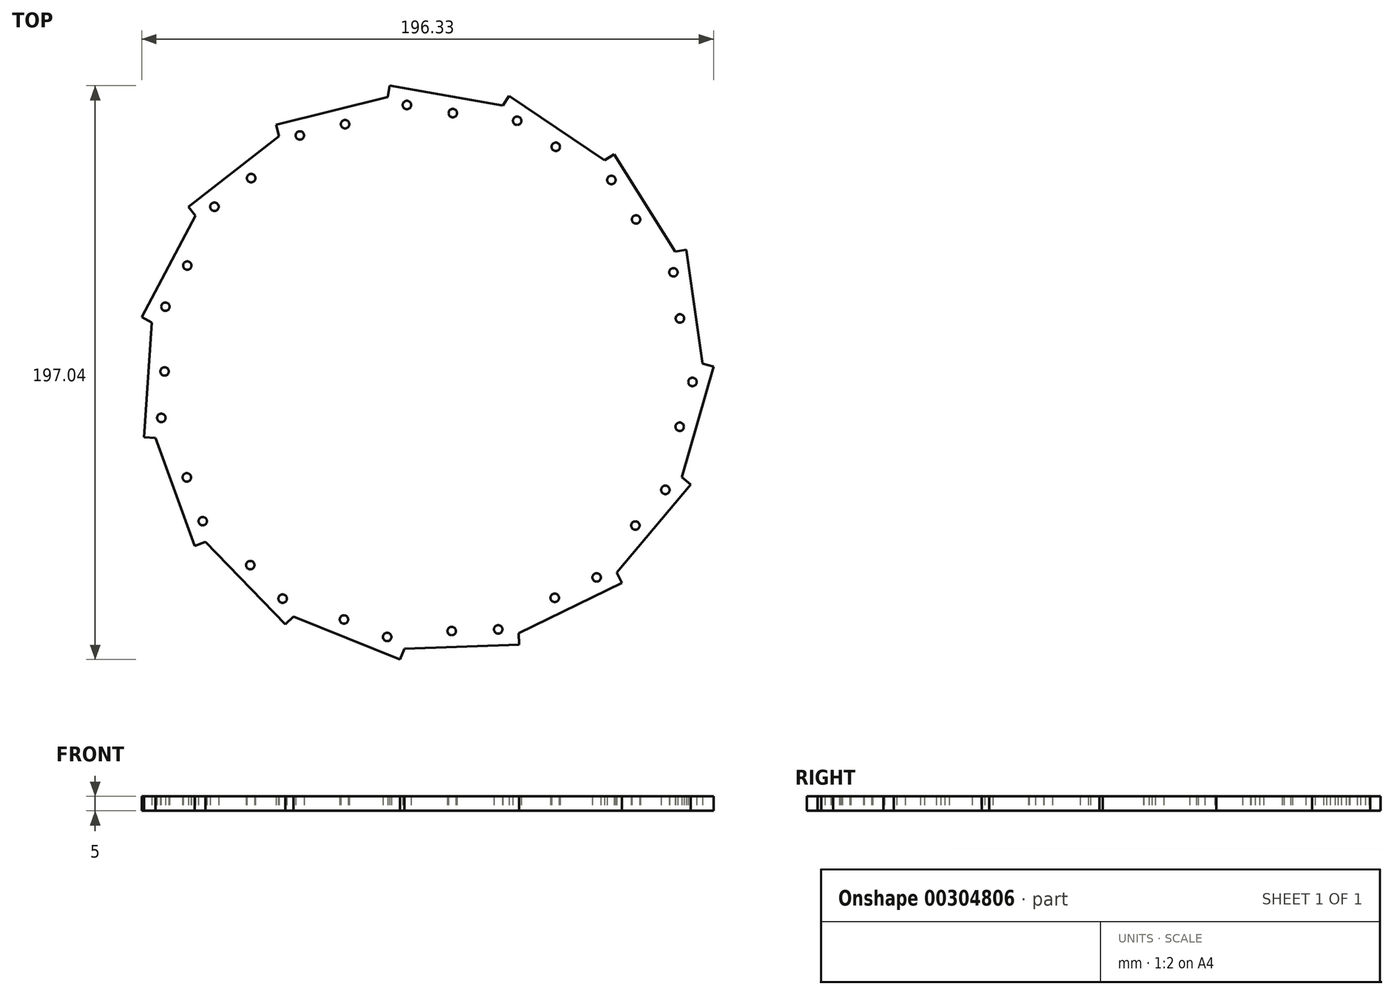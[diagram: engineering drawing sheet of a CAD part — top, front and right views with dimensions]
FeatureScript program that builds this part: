
annotation { "Feature Type Name" : "Feature", "Feature Type Description" : "" }
export const myFeature = defineFeature(function(context is Context, id is Id, definition is map)
    precondition{}
    {
        {
            var Q0;
            Q0=qCreatedBy(makeId("Top.planeOp"),FACE);
            var sketch = newSketch(context, id + "F0", { "sketchPlane" : qUnion([Q0])});
            skCircle(sketch, "E0.1.6", {"center": v(-42.97, 81.25) * mm, "radius": 1.45 * mm});
            skCircle(sketch, "E0.1.14", {"center": v(-27.44, 85.12) * mm, "radius": 1.45 * mm});
            skPoint(sketch, "E0.center", {"position": v(0, 0) * mm});
            skLineSegment(sketch, "E1", {"start": v(-51.1, 84.9) * mm, "end": v(-12.83, 94.43) * mm});
            skLineSegment(sketch, "E2", {"start": v(-12.83, 94.43) * mm, "end": v(-12.15, 98.33) * mm});
            skLineSegment(sketch, "E3.1.0", {"start": v(-81.2, 56.77) * mm, "end": v(-50.13, 81.04) * mm});
            skCircle(sketch, "E3.1.1", {"center": v(-72.3, 56.75) * mm, "radius": 1.45 * mm});
            skCircle(sketch, "E3.1.2", {"center": v(-59.7, 66.6) * mm, "radius": 1.45 * mm});
            skLineSegment(sketch, "E3.1.3", {"start": v(-50.13, 81.04) * mm, "end": v(-51.1, 84.9) * mm});
            skLineSegment(sketch, "E3.2.0", {"start": v(-97.27, 18.83) * mm, "end": v(-78.76, 53.65) * mm});
            skCircle(sketch, "E3.2.1", {"center": v(-89.13, 22.43) * mm, "radius": 1.45 * mm});
            skCircle(sketch, "E3.2.2", {"center": v(-81.62, 36.56) * mm, "radius": 1.45 * mm});
            skLineSegment(sketch, "E3.2.3", {"start": v(-78.76, 53.65) * mm, "end": v(-81.2, 56.77) * mm});
            skLineSegment(sketch, "E3.3.0", {"start": v(-96.52, -22.36) * mm, "end": v(-93.77, 16.97) * mm});
            skCircle(sketch, "E3.3.1", {"center": v(-90.55, -15.76) * mm, "radius": 1.45 * mm});
            skCircle(sketch, "E3.3.2", {"center": v(-89.43, 0.2) * mm, "radius": 1.45 * mm});
            skLineSegment(sketch, "E3.3.3", {"start": v(-93.77, 16.97) * mm, "end": v(-97.27, 18.83) * mm});
            skLineSegment(sketch, "E3.4.0", {"start": v(-79.08, -59.69) * mm, "end": v(-92.57, -22.63) * mm});
            skCircle(sketch, "E3.4.1", {"center": v(-76.31, -51.23) * mm, "radius": 1.45 * mm});
            skCircle(sketch, "E3.4.2", {"center": v(-81.78, -36.2) * mm, "radius": 1.45 * mm});
            skLineSegment(sketch, "E3.4.3", {"start": v(-92.57, -22.63) * mm, "end": v(-96.52, -22.36) * mm});
            skLineSegment(sketch, "E3.5.0", {"start": v(-47.97, -86.7) * mm, "end": v(-75.36, -58.33) * mm});
            skCircle(sketch, "E3.5.1", {"center": v(-48.88, -77.84) * mm, "radius": 1.45 * mm});
            skCircle(sketch, "E3.5.2", {"center": v(-60, -66.33) * mm, "radius": 1.45 * mm});
            skLineSegment(sketch, "E3.5.3", {"start": v(-75.36, -58.33) * mm, "end": v(-79.08, -59.69) * mm});
            skLineSegment(sketch, "E3.6.0", {"start": v(-8.56, -98.7) * mm, "end": v(-45.12, -83.94) * mm});
            skCircle(sketch, "E3.6.1", {"center": v(-13, -90.99) * mm, "radius": 1.45 * mm});
            skCircle(sketch, "E3.6.2", {"center": v(-27.83, -85) * mm, "radius": 1.45 * mm});
            skLineSegment(sketch, "E3.6.3", {"start": v(-45.12, -83.94) * mm, "end": v(-47.97, -86.7) * mm});
            skLineSegment(sketch, "E3.7.0", {"start": v(32.33, -93.66) * mm, "end": v(-7.08, -95.03) * mm});
            skCircle(sketch, "E3.7.1", {"center": v(25.14, -88.4) * mm, "radius": 1.45 * mm});
            skCircle(sketch, "E3.7.2", {"center": v(9.15, -88.96) * mm, "radius": 1.45 * mm});
            skLineSegment(sketch, "E3.7.3", {"start": v(-7.08, -95.03) * mm, "end": v(-8.56, -98.7) * mm});
            skLineSegment(sketch, "E3.8.0", {"start": v(67.63, -72.41) * mm, "end": v(32.19, -89.7) * mm});
            skCircle(sketch, "E3.8.1", {"center": v(58.92, -70.54) * mm, "radius": 1.45 * mm});
            skCircle(sketch, "E3.8.2", {"center": v(44.54, -77.55) * mm, "radius": 1.45 * mm});
            skLineSegment(sketch, "E3.8.3", {"start": v(32.19, -89.7) * mm, "end": v(32.33, -93.66) * mm});
            skLineSegment(sketch, "E3.9.0", {"start": v(91.23, -38.65) * mm, "end": v(65.89, -68.85) * mm});
            skCircle(sketch, "E3.9.1", {"center": v(82.52, -40.47) * mm, "radius": 1.45 * mm});
            skCircle(sketch, "E3.9.2", {"center": v(72.23, -52.73) * mm, "radius": 1.45 * mm});
            skLineSegment(sketch, "E3.9.3", {"start": v(65.89, -68.85) * mm, "end": v(67.63, -72.41) * mm});
            skLineSegment(sketch, "E3.10.0", {"start": v(99.06, 1.8) * mm, "end": v(88.2, -36.1) * mm});
            skCircle(sketch, "E3.10.1", {"center": v(91.85, -3.41) * mm, "radius": 1.45 * mm});
            skCircle(sketch, "E3.10.2", {"center": v(87.44, -18.8) * mm, "radius": 1.45 * mm});
            skLineSegment(sketch, "E3.10.3", {"start": v(88.2, -36.1) * mm, "end": v(91.23, -38.65) * mm});
            skLineSegment(sketch, "E3.11.0", {"start": v(89.77, 41.94) * mm, "end": v(95.25, 2.9) * mm});
            skCircle(sketch, "E3.11.1", {"center": v(85.3, 34.24) * mm, "radius": 1.45 * mm});
            skCircle(sketch, "E3.11.2", {"center": v(87.52, 18.4) * mm, "radius": 1.45 * mm});
            skLineSegment(sketch, "E3.11.3", {"start": v(95.25, 2.9) * mm, "end": v(99.06, 1.8) * mm});
            skLineSegment(sketch, "E3.12.0", {"start": v(64.95, 74.82) * mm, "end": v(85.84, 41.39) * mm});
            skCircle(sketch, "E3.12.1", {"center": v(64, 65.97) * mm, "radius": 1.45 * mm});
            skCircle(sketch, "E3.12.2", {"center": v(72.47, 52.4) * mm, "radius": 1.45 * mm});
            skLineSegment(sketch, "E3.12.3", {"start": v(85.84, 41.39) * mm, "end": v(89.77, 41.94) * mm});
            skLineSegment(sketch, "E3.13.0", {"start": v(28.9, 94.77) * mm, "end": v(61.59, 72.72) * mm});
            skCircle(sketch, "E3.13.1", {"center": v(31.63, 86.3) * mm, "radius": 1.45 * mm});
            skCircle(sketch, "E3.13.2", {"center": v(44.9, 77.35) * mm, "radius": 1.45 * mm});
            skLineSegment(sketch, "E3.13.3", {"start": v(61.59, 72.72) * mm, "end": v(64.95, 74.82) * mm});
            skLineSegment(sketch, "E3.14.0", {"start": v(-12.15, 98.33) * mm, "end": v(26.68, 91.49) * mm});
            skCircle(sketch, "E3.14.1", {"center": v(-6.2, 91.7) * mm, "radius": 1.45 * mm});
            skCircle(sketch, "E3.14.2", {"center": v(9.55, 88.92) * mm, "radius": 1.45 * mm});
            skLineSegment(sketch, "E3.14.3", {"start": v(26.68, 91.49) * mm, "end": v(28.9, 94.77) * mm});
            skSolve(sketch);
        }
        {
            var Q0;
            Q0=makeQuery(id+"F0.imprint","IMPRINT",FACE,{"disambiguationData":[TD([[makeQuery(id+"F0.imprint","IMPRINT",EDGE,{"derivedFrom":sQuery(id+"F0.wireOp",EDGE,"E0.1.6")}),-1.0]])]});
            extrude(context, id + "F1", {"entities" : qUnion([Q0]), "depth" : 5 * mm});
        }
    });
